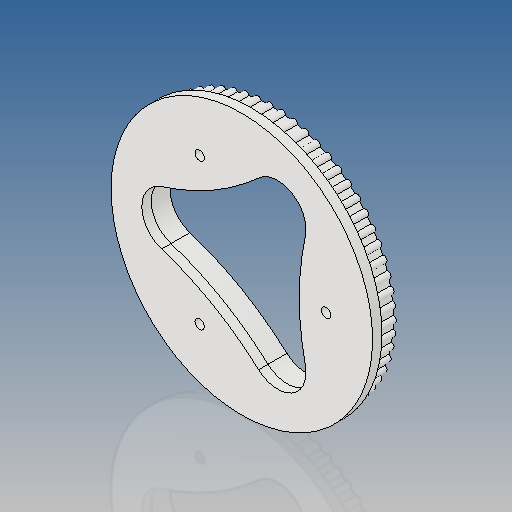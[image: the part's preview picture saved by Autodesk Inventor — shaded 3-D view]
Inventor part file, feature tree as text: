
AUTODESK INVENTOR PART (.ipt)
format: ipt  version: 2017 (Build 210142000, 142)  size: 356,864 bytes
history: native  units: mm
features: other x5, extrude x3, sketch x3, reference x1
ambient origin geometry x8: Origin, YZ Plane, XZ Plane, XY Plane, X Axis, Y Axis, Z Axis, Center Point
bodies: Body1 (feature_tree), Body2 (feature_tree)
feature tree (12):
  other  "Sólido1"
  extrude  "Extrusión1"  Depth=6.0mm TaperAngle=0.0deg
  extrude  "Extrusión2"  Depth=3.0mm
  extrude  "Extrusión3"  Depth=3.0mm
  sketch  "Boceto1"  dims[d0=78.21mm d1=6.0mm d2=0.0mm]
  reference  "Referencia1"
  sketch  "Boceto2"  dims[d4=3.0mm d5=0.0mm d6=5.5mm]
  other  "Sólido2"
  sketch  "Boceto3"  dims[d7=3.0mm d8=0.0mm d9=2.0mm d11=72.0mm d20=68.564981mm d21=138.198275mm d22=70.618372mm d23=25.06771mm d24=640.0mm d26=360.0deg d28=3.837583mm d30=83.0mm]
  other  "Sólido3"
  other  "conjunto polea plato-carrete.iam"
  other  "Carrete Impreso:1"
